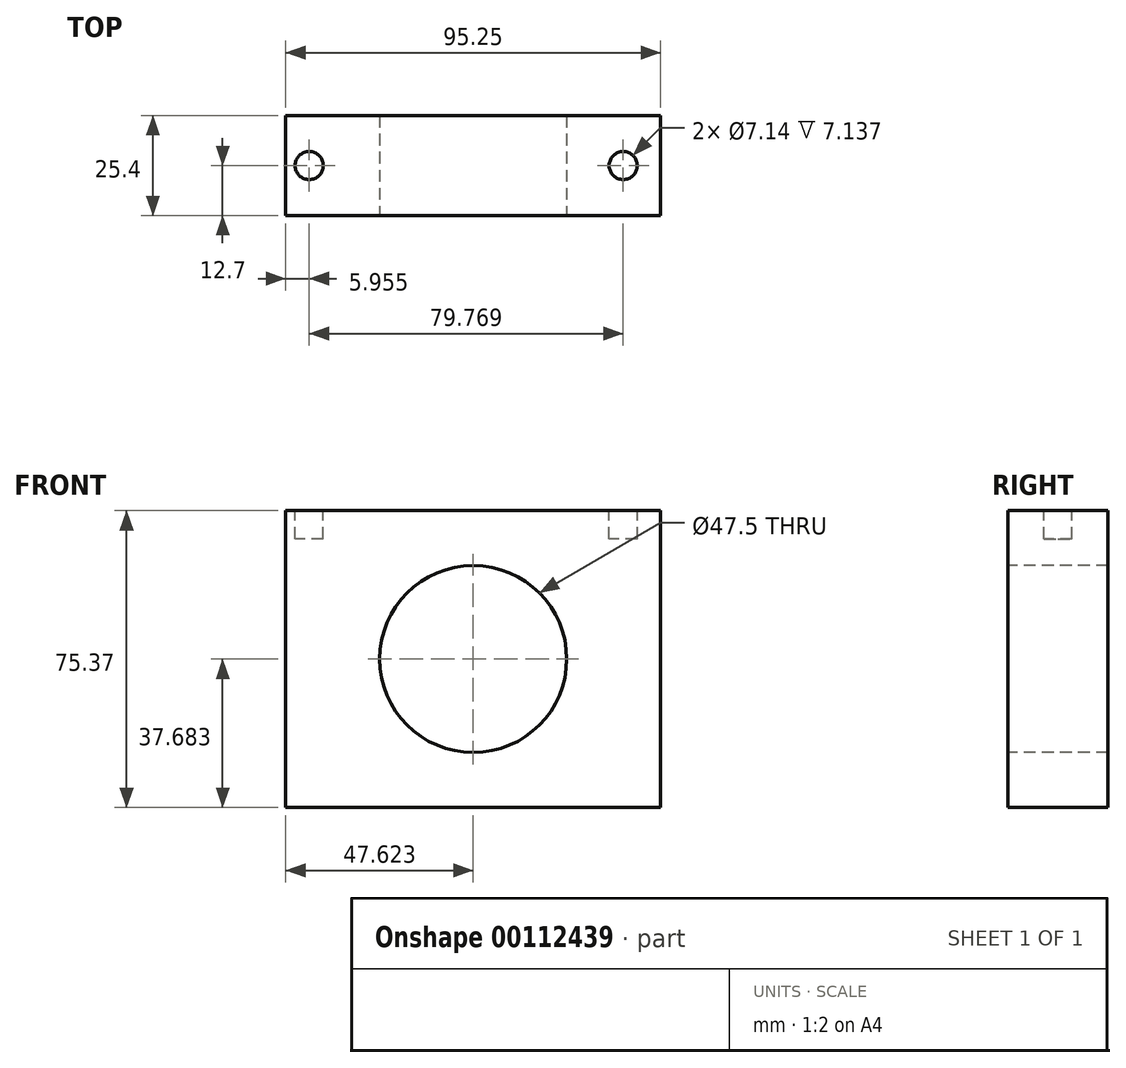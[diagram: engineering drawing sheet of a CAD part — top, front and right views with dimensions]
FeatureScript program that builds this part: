
annotation { "Feature Type Name" : "Feature", "Feature Type Description" : "" }
export const myFeature = defineFeature(function(context is Context, id is Id, definition is map)
    precondition{}
    {
        {
            var Q0;
            Q0=qCreatedBy(makeId("Front.planeOp"),FACE);
            var sketch = newSketch(context, id + "F0", { "sketchPlane" : qUnion([Q0])});
            skLineSegment(sketch, "E0", {"start": v(-29.5, 23.76) * mm, "end": v(-29.5, -51.61) * mm});
            skLineSegment(sketch, "E1", {"start": v(-29.5, -51.61) * mm, "end": v(65.76, -51.61) * mm});
            skLineSegment(sketch, "E2", {"start": v(-29.5, 23.76) * mm, "end": v(65.76, 23.76) * mm});
            skLineSegment(sketch, "E3", {"start": v(65.76, -51.61) * mm, "end": v(65.76, 23.76) * mm});
            skPoint(sketch, "E4.centerSnap0", {"position": v(65.76, -13.93) * mm});
            skPoint(sketch, "E4.centerSnap1", {"position": v(18.13, 23.76) * mm});
            skCircle(sketch, "E5", {"center": v(18.13, -13.93) * mm, "radius": 23.75 * mm});
            skPoint(sketch, "E5.centerSnap0", {"position": v(-29.5, -13.93) * mm});
            skSolve(sketch);
        }
        {
            var Q0;
            Q0=makeQuery(id+"F0.imprint","IMPRINT",FACE,{"disambiguationData":[TD([[makeQuery(id+"F0.imprint","IMPRINT",EDGE,{"derivedFrom":sQuery(id+"F0.wireOp",EDGE,"E0")}),1.0]])]});
            extrude(context, id + "F1", {"entities" : qUnion([Q0]), "oppositeDirection" : true, "depth" : 25.4 * mm});
        }
        {
            var Q0;
            Q0=makeQuery(id+"F1.opExtrude","SWEPT_FACE",FACE,{"disambiguationData":[OSD([sQuery(id+"F0.wireOp",EDGE,"E2")])]});
            var sketch = newSketch(context, id + "F2", { "sketchPlane" : qUnion([Q0])});
            skLineSegment(sketch, "E6", {"start": v(65.76, 12.7) * mm, "end": v(56.23, 12.7) * mm, "construction": true});
            skCircle(sketch, "E7", {"center": v(56.23, 12.7) * mm, "radius": 3.57 * mm});
            skLineSegment(sketch, "E8", {"start": v(52.66, 12.7) * mm, "end": v(-23.54, 12.7) * mm, "construction": true});
            skCircle(sketch, "E9", {"center": v(-23.54, 12.7) * mm, "radius": 3.57 * mm});
            skSolve(sketch);
        }
        {
            var Q0;
            Q0=makeQuery(id+"F2.imprint","IMPRINT",FACE,{"disambiguationData":[TD([[makeQuery(id+"F2.imprint","IMPRINT",EDGE,{"derivedFrom":sQuery(id+"F2.wireOp",EDGE,"E9")}),1.0]])]});
            var Q1;
            Q1=makeQuery(id+"F2.imprint","IMPRINT",FACE,{"disambiguationData":[TD([[makeQuery(id+"F2.imprint","IMPRINT",EDGE,{"derivedFrom":sQuery(id+"F2.wireOp",EDGE,"E7")}),1.0]])]});
            extrude(context, id + "F3", {"entities" : qUnion([Q0, Q1]), "operationType" : NewBodyOperationType.REMOVE, "oppositeDirection" : true, "depth" : 7.14 * mm});
        }
    });
